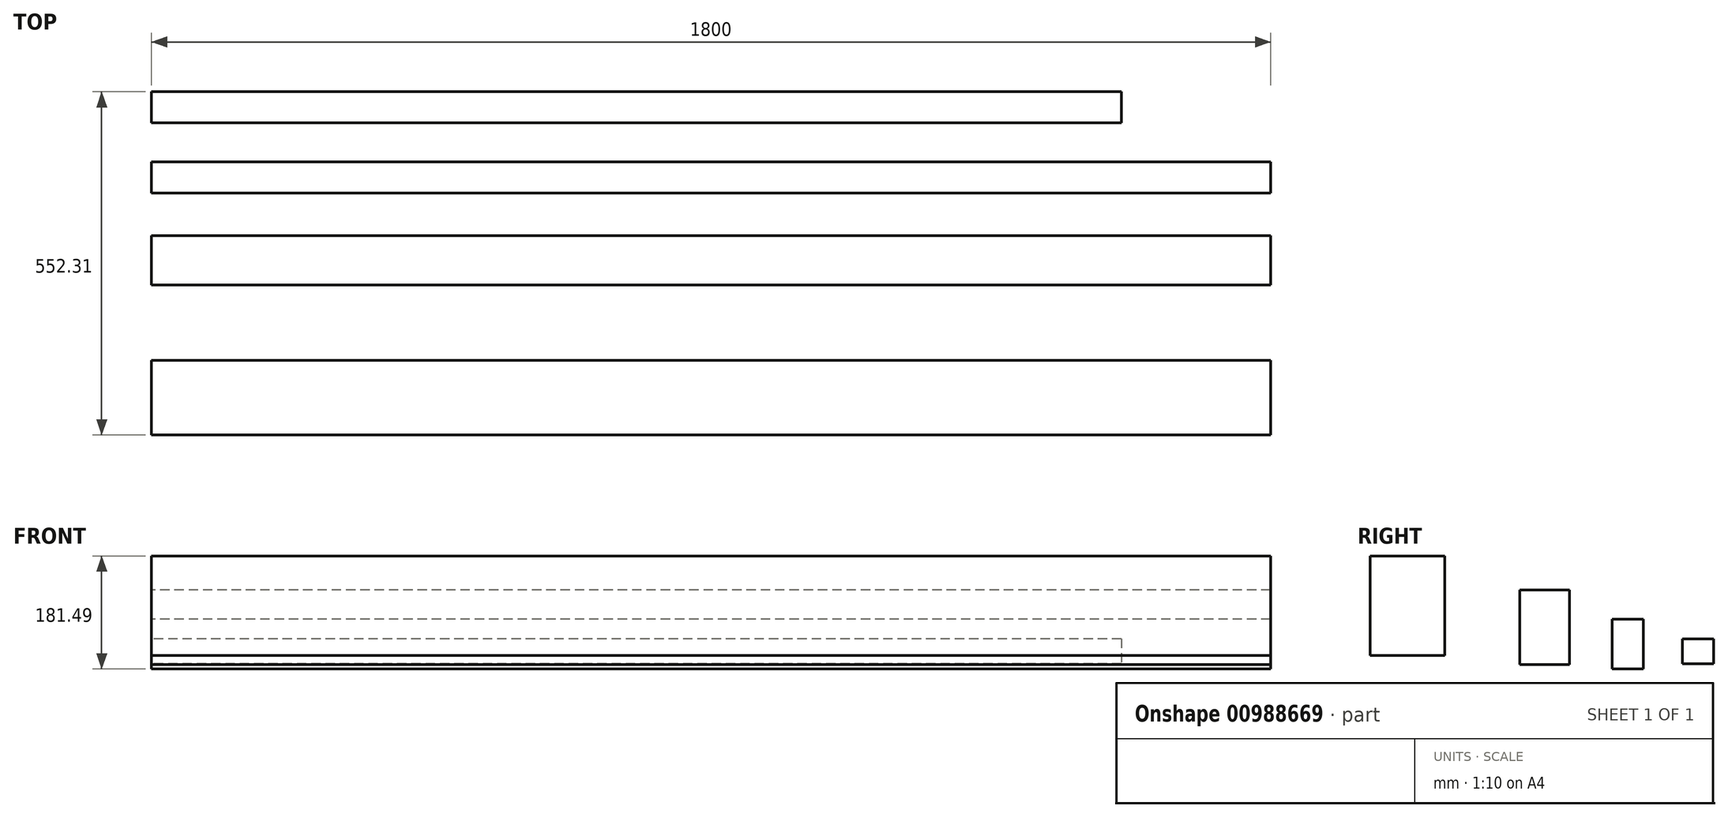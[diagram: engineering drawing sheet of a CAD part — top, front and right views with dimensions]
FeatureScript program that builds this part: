
annotation { "Feature Type Name" : "Feature", "Feature Type Description" : "" }
export const myFeature = defineFeature(function(context is Context, id is Id, definition is map)
    precondition{}
    {
        {
            var Q0;
            Q0=qCreatedBy(makeId("Right.planeOp"),FACE);
            var sketch = newSketch(context, id + "F0", { "sketchPlane" : qUnion([Q0])});
            skLineSegment(sketch, "E0.bottom", {"start": v(-140.34, 181.49) * mm, "end": v(-20.34, 181.49) * mm});
            skLineSegment(sketch, "E0.top", {"start": v(-140.34, 21.49) * mm, "end": v(-20.34, 21.49) * mm});
            skLineSegment(sketch, "E0.left", {"start": v(-140.34, 181.49) * mm, "end": v(-140.34, 21.49) * mm});
            skLineSegment(sketch, "E0.right", {"start": v(-20.34, 181.49) * mm, "end": v(-20.34, 21.49) * mm});
            skLineSegment(sketch, "E1.bottom", {"start": v(100.63, 126.76) * mm, "end": v(180.63, 126.76) * mm});
            skLineSegment(sketch, "E1.top", {"start": v(100.63, 6.76) * mm, "end": v(180.63, 6.76) * mm});
            skLineSegment(sketch, "E1.left", {"start": v(100.63, 126.76) * mm, "end": v(100.63, 6.76) * mm});
            skLineSegment(sketch, "E1.right", {"start": v(180.63, 126.76) * mm, "end": v(180.63, 6.76) * mm});
            skLineSegment(sketch, "E2.bottom", {"start": v(249.21, 80) * mm, "end": v(299.21, 80) * mm});
            skLineSegment(sketch, "E2.top", {"start": v(249.21, 0) * mm, "end": v(299.21, 0) * mm});
            skLineSegment(sketch, "E2.left", {"start": v(249.21, 80) * mm, "end": v(249.21, 0) * mm});
            skLineSegment(sketch, "E2.right", {"start": v(299.21, 80) * mm, "end": v(299.21, 0) * mm});
            skLineSegment(sketch, "E3.bottom", {"start": v(361.97, 48.4) * mm, "end": v(411.97, 48.4) * mm});
            skLineSegment(sketch, "E3.top", {"start": v(361.97, 8.4) * mm, "end": v(411.97, 8.4) * mm});
            skLineSegment(sketch, "E3.left", {"start": v(361.97, 48.4) * mm, "end": v(361.97, 8.4) * mm});
            skLineSegment(sketch, "E3.right", {"start": v(411.97, 48.4) * mm, "end": v(411.97, 8.4) * mm});
            skSolve(sketch);
        }
        {
            var Q0;
            Q0=makeQuery(id+"F0.imprint","IMPRINT",FACE,{"disambiguationData":[TD([[makeQuery(id+"F0.imprint","IMPRINT",EDGE,{"derivedFrom":sQuery(id+"F0.wireOp",EDGE,"E0.bottom")}),-1.0]])]});
            var Q1;
            Q1=makeQuery(id+"F0.imprint","IMPRINT",FACE,{"disambiguationData":[TD([[makeQuery(id+"F0.imprint","IMPRINT",EDGE,{"derivedFrom":sQuery(id+"F0.wireOp",EDGE,"E1.bottom")}),-1.0]])]});
            var Q2;
            Q2=makeQuery(id+"F0.imprint","IMPRINT",FACE,{"disambiguationData":[TD([[makeQuery(id+"F0.imprint","IMPRINT",EDGE,{"derivedFrom":sQuery(id+"F0.wireOp",EDGE,"E2.bottom")}),-1.0]])]});
            extrude(context, id + "F1", {"entities" : qUnion([Q0, Q1, Q2]), "depth" : 1800 * mm, "offsetDistance" : 25 * mm});
        }
        {
            var Q0;
            Q0=makeQuery(id+"F0.imprint","IMPRINT",FACE,{"disambiguationData":[TD([[makeQuery(id+"F0.imprint","IMPRINT",EDGE,{"derivedFrom":sQuery(id+"F0.wireOp",EDGE,"E3.bottom")}),-1.0]])]});
            extrude(context, id + "F2", {"entities" : qUnion([Q0]), "depth" : 1560 * mm, "offsetDistance" : 25 * mm});
        }
    });
